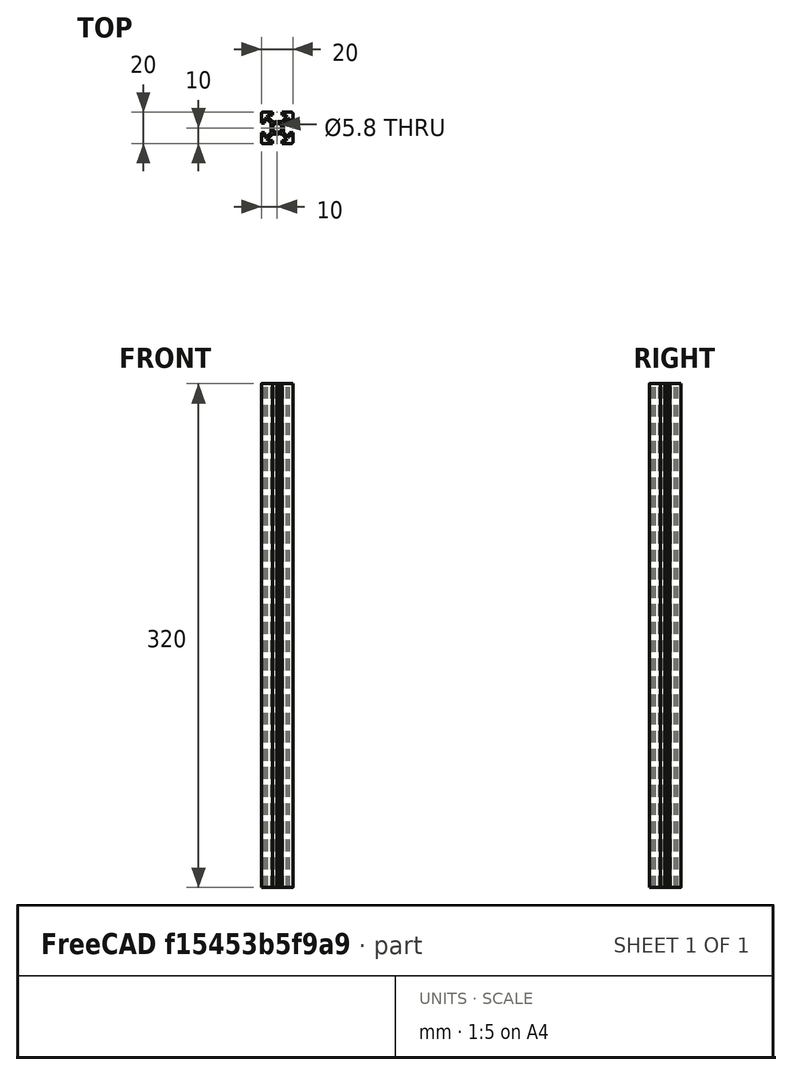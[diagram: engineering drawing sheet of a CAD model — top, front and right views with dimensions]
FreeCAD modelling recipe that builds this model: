
FCSTD DOCUMENT  (FreeCAD 0.17R13387 (Git))
Label: Y-Profile_2020
License: All rights reserved
LicenseURL: http://en.wikipedia.org/wiki/All_rights_reserved
objects: Sketcher::SketchObject×1, PartDesign::Pad×1, PartDesign::Body×1
note: 4 computed .brp shape members not serialized (recipe doc carries the construction recipe); baked Part::Feature solids carry a one-line shape summary decoded from their .brp

FEATURE [Sketcher::SketchObject] Sketch001
  sketch-geometry (77):
    g0: LineSegment StartX=-8 StartY=-3 StartZ=0 EndX=-10 EndY=-3 EndZ=0
    g1: LineSegment StartX=-10 StartY=-3 StartZ=0 EndX=-10 EndY=-9 EndZ=0
    g2: ArcOfCircle CenterX=-9 CenterY=-9 CenterZ=0 NormalX=0 NormalY=0 NormalZ=1 AngleXU=0 Radius=1 StartAngle=3.14159 EndAngle=4.71239
    g3: LineSegment StartX=-9 StartY=-10 StartZ=0 EndX=-3 EndY=-10 EndZ=0
    g4: LineSegment StartX=-3 StartY=-10 StartZ=0 EndX=-3 EndY=-8 EndZ=0
    g5: LineSegment StartX=-3 StartY=-8 StartZ=0 EndX=-6 EndY=-8 EndZ=0
    g6: LineSegment StartX=-6 StartY=-8 StartZ=0 EndX=-6 EndY=-7.06066 EndZ=0
    g7: LineSegment StartX=-6 StartY=-7.06066 StartZ=0 EndX=-2.93934 EndY=-4 EndZ=0
    g8: LineSegment StartX=-2.93934 StartY=-4 StartZ=0 EndX=-0.65359 EndY=-4 EndZ=0
    g9: ArcOfCircle CenterX=-0.65359 CenterY=-3.5 CenterZ=0 NormalX=0 NormalY=0 NormalZ=1 AngleXU=0 Radius=0.5 StartAngle=4.71239 EndAngle=5.23599
    g10: LineSegment StartX=-0.40359 StartY=-3.93301 StartZ=0 EndX=0 EndY=-3.7 EndZ=0
    g11: LineSegment StartX=0 StartY=-3.7 StartZ=0 EndX=0.40359 EndY=-3.93301 EndZ=0
    g12: ArcOfCircle CenterX=0.65359 CenterY=-3.5 CenterZ=0 NormalX=0 NormalY=0 NormalZ=1 AngleXU=0 Radius=0.5 StartAngle=4.18879 EndAngle=5.23599
    g13: LineSegment StartX=0.90359 StartY=-3.93301 StartZ=0 EndX=1.21889 EndY=-3.75098 EndZ=0
    g14: LineSegment StartX=1.21889 StartY=-3.75098 StartZ=0 EndX=2.5 EndY=-4 EndZ=0
    g15: LineSegment StartX=2.5 StartY=-4 StartZ=0 EndX=2.93934 EndY=-4 EndZ=0
    g16: LineSegment StartX=2.93934 StartY=-4 StartZ=0 EndX=6 EndY=-7.06066 EndZ=0
    g17: LineSegment StartX=6 StartY=-7.06066 StartZ=0 EndX=6 EndY=-8 EndZ=0
    g18: LineSegment StartX=6 StartY=-8 StartZ=0 EndX=3 EndY=-8 EndZ=0
    g19: LineSegment StartX=3 StartY=-8 StartZ=0 EndX=3 EndY=-10 EndZ=0
    g20: LineSegment StartX=3 StartY=-10 StartZ=0 EndX=9 EndY=-10 EndZ=0
    g21: ArcOfCircle CenterX=9 CenterY=-9 CenterZ=0 NormalX=0 NormalY=0 NormalZ=1 AngleXU=0 Radius=1 StartAngle=4.71239 EndAngle=6.28319
    g22: LineSegment StartX=10 StartY=-9 StartZ=0 EndX=10 EndY=-3 EndZ=0
    g23: LineSegment StartX=10 StartY=-3 StartZ=0 EndX=8 EndY=-3 EndZ=0
    g24: LineSegment StartX=8 StartY=-3 StartZ=0 EndX=8 EndY=-6 EndZ=0
    g25: LineSegment StartX=8 StartY=-6 StartZ=0 EndX=7.06066 EndY=-6 EndZ=0
    g26: LineSegment StartX=7.06066 StartY=-6 StartZ=0 EndX=4 EndY=-2.93934 EndZ=0
    g27: LineSegment StartX=4 StartY=-2.93934 StartZ=0 EndX=4 EndY=-0.65359 EndZ=0
    g28: ArcOfCircle CenterX=3.5 CenterY=-0.65359 CenterZ=0 NormalX=0 NormalY=0 NormalZ=1 AngleXU=0 Radius=0.5 StartAngle=0 EndAngle=0.523599
    g29: LineSegment StartX=3.93301 StartY=-0.40359 StartZ=0 EndX=3.7 EndY=0 EndZ=0
    g30: LineSegment StartX=3.7 StartY=0 StartZ=0 EndX=3.93301 EndY=0.40359 EndZ=0
    g31: ArcOfCircle CenterX=3.5 CenterY=0.65359 CenterZ=0 NormalX=0 NormalY=0 NormalZ=1 AngleXU=0 Radius=0.5 StartAngle=5.75959 EndAngle=6.80678
    g32: LineSegment StartX=3.93301 StartY=0.90359 StartZ=0 EndX=3.75098 EndY=1.21889 EndZ=0
    g33: LineSegment StartX=3.75098 StartY=1.21889 StartZ=0 EndX=4 EndY=2.5 EndZ=0
    g34: LineSegment StartX=4 StartY=2.5 StartZ=0 EndX=4 EndY=2.93934 EndZ=0
    g35: LineSegment StartX=4 StartY=2.93934 StartZ=0 EndX=7.06066 EndY=6 EndZ=0
    g36: LineSegment StartX=7.06066 StartY=6 StartZ=0 EndX=8 EndY=6 EndZ=0
    g37: LineSegment StartX=8 StartY=6 StartZ=0 EndX=8 EndY=3 EndZ=0
    g38: LineSegment StartX=8 StartY=3 StartZ=0 EndX=10 EndY=3 EndZ=0
    g39: LineSegment StartX=10 StartY=3 StartZ=0 EndX=10 EndY=9 EndZ=0
    g40: ArcOfCircle CenterX=9 CenterY=9 CenterZ=0 NormalX=0 NormalY=0 NormalZ=1 AngleXU=0 Radius=1 StartAngle=0 EndAngle=1.5708
    g41: LineSegment StartX=9 StartY=10 StartZ=0 EndX=3 EndY=10 EndZ=0
    g42: LineSegment StartX=3 StartY=10 StartZ=0 EndX=3 EndY=8 EndZ=0
    g43: LineSegment StartX=3 StartY=8 StartZ=0 EndX=6 EndY=8 EndZ=0
    g44: LineSegment StartX=6 StartY=8 StartZ=0 EndX=6 EndY=7.06066 EndZ=0
    g45: LineSegment StartX=6 StartY=7.06066 StartZ=0 EndX=2.93934 EndY=4 EndZ=0
    g46: LineSegment StartX=2.93934 StartY=4 StartZ=0 EndX=0.65359 EndY=4 EndZ=0
    g47: ArcOfCircle CenterX=0.65359 CenterY=3.5 CenterZ=0 NormalX=0 NormalY=0 NormalZ=1 AngleXU=0 Radius=0.5 StartAngle=1.5708 EndAngle=2.0944
    g48: LineSegment StartX=0.40359 StartY=3.93301 StartZ=0 EndX=0 EndY=3.7 EndZ=0
    g49: LineSegment StartX=0 StartY=3.7 StartZ=0 EndX=-0.40359 EndY=3.93301 EndZ=0
    g50: ArcOfCircle CenterX=-0.65359 CenterY=3.5 CenterZ=0 NormalX=0 NormalY=0 NormalZ=1 AngleXU=0 Radius=0.5 StartAngle=1.0472 EndAngle=2.0944
    g51: LineSegment StartX=-0.90359 StartY=3.93301 StartZ=0 EndX=-1.21889 EndY=3.75098 EndZ=0
    g52: LineSegment StartX=-1.21889 StartY=3.75098 StartZ=0 EndX=-2.5 EndY=4 EndZ=0
    g53: LineSegment StartX=-2.5 StartY=4 StartZ=0 EndX=-2.93934 EndY=4 EndZ=0
    g54: LineSegment StartX=-2.93934 StartY=4 StartZ=0 EndX=-6 EndY=7.06066 EndZ=0
    g55: LineSegment StartX=-6 StartY=7.06066 StartZ=0 EndX=-6 EndY=8 EndZ=0
    g56: LineSegment StartX=-6 StartY=8 StartZ=0 EndX=-3 EndY=8 EndZ=0
    g57: LineSegment StartX=-3 StartY=8 StartZ=0 EndX=-3 EndY=10 EndZ=0
    g58: LineSegment StartX=-3 StartY=10 StartZ=0 EndX=-9 EndY=10 EndZ=0
    g59: ArcOfCircle CenterX=-9 CenterY=9 CenterZ=0 NormalX=0 NormalY=0 NormalZ=1 AngleXU=0 Radius=1 StartAngle=1.5708 EndAngle=3.14159
    g60: LineSegment StartX=-10 StartY=9 StartZ=0 EndX=-10 EndY=3 EndZ=0
    g61: LineSegment StartX=-10 StartY=3 StartZ=0 EndX=-8 EndY=3 EndZ=0
    g62: LineSegment StartX=-8 StartY=3 StartZ=0 EndX=-8 EndY=6 EndZ=0
    g63: LineSegment StartX=-8 StartY=6 StartZ=0 EndX=-7.06066 EndY=6 EndZ=0
    g64: LineSegment StartX=-7.06066 StartY=6 StartZ=0 EndX=-4 EndY=2.93934 EndZ=0
    g65: LineSegment StartX=-4 StartY=2.93934 StartZ=0 EndX=-4 EndY=0.65359 EndZ=0
    g66: ArcOfCircle CenterX=-3.5 CenterY=0.65359 CenterZ=0 NormalX=0 NormalY=0 NormalZ=1 AngleXU=0 Radius=0.5 StartAngle=3.14159 EndAngle=3.66519
    g67: LineSegment StartX=-3.93301 StartY=0.40359 StartZ=0 EndX=-3.7 EndY=0 EndZ=0
    g68: LineSegment StartX=-3.7 StartY=0 StartZ=0 EndX=-3.93301 EndY=-0.40359 EndZ=0
    g69: ArcOfCircle CenterX=-3.5 CenterY=-0.65359 CenterZ=0 NormalX=0 NormalY=0 NormalZ=1 AngleXU=0 Radius=0.5 StartAngle=2.61799 EndAngle=3.66519
    g70: LineSegment StartX=-3.93301 StartY=-0.90359 StartZ=0 EndX=-3.75098 EndY=-1.21889 EndZ=0
    g71: LineSegment StartX=-3.75098 StartY=-1.21889 StartZ=0 EndX=-4 EndY=-2.5 EndZ=0
    g72: LineSegment StartX=-4 StartY=-2.5 StartZ=0 EndX=-4 EndY=-2.93934 EndZ=0
    g73: LineSegment StartX=-4 StartY=-2.93934 StartZ=0 EndX=-7.06066 EndY=-6 EndZ=0
    g74: LineSegment StartX=-7.06066 StartY=-6 StartZ=0 EndX=-8 EndY=-6 EndZ=0
    g75: LineSegment StartX=-8 StartY=-6 StartZ=0 EndX=-8 EndY=-3 EndZ=0
    g76: Circle CenterX=0 CenterY=0 CenterZ=0 NormalX=0 NormalY=0 NormalZ=1 AngleXU=0 Radius=2.9
  constraints (105):
    c: Horizontal(g0)
    c: Coincident(g0,g1)
    c: Vertical(g1)
    c: Coincident(g1,g2)
    c: Coincident(g2,g3)
    c: Horizontal(g3)
    c: Coincident(g3,g4)
    c: Coincident(g4,g5)
    c: Horizontal(g5)
    c: Coincident(g5,g6)
    c: Coincident(g6,g7)
    c: Coincident(g7,g8)
    c: Horizontal(g8)
    c: Coincident(g8,g9)
    c: Coincident(g9,g10)
    c: Coincident(g10,g11)
    c: Coincident(g11,g12)
    c: Coincident(g12,g13)
    c: Coincident(g13,g14)
    c: Coincident(g14,g15)
    c: Horizontal(g15)
    c: Coincident(g15,g16)
    c: Coincident(g16,g17)
    c: Coincident(g17,g18)
    c: Coincident(g18,g19)
    c: Vertical(g19)
    c: Coincident(g19,g20)
    c: Horizontal(g20)
    c: Coincident(g20,g21)
    c: Coincident(g21,g22)
    c: Vertical(g22)
    c: Coincident(g22,g23)
    c: Horizontal(g23)
    c: Coincident(g23,g24)
    c: Vertical(g24)
    c: Coincident(g24,g25)
    c: Coincident(g25,g26)
    c: Coincident(g26,g27)
    c: Vertical(g27)
    c: Coincident(g27,g28)
    c: Coincident(g28,g29)
    c: Coincident(g29,g30)
    c: Coincident(g30,g31)
    c: Coincident(g31,g32)
    c: Coincident(g32,g33)
    c: Coincident(g33,g34)
    c: Vertical(g34)
    c: Coincident(g34,g35)
    c: Coincident(g35,g36)
    c: Coincident(g36,g37)
    c: Coincident(g37,g38)
    c: Horizontal(g38)
    c: Coincident(g38,g39)
    c: Vertical(g39)
    c: Coincident(g39,g40)
    c: Coincident(g40,g41)
    c: Horizontal(g41)
    c: Coincident(g41,g42)
    c: Coincident(g42,g43)
    c: Horizontal(g43)
    c: Coincident(g43,g44)
    c: Coincident(g44,g45)
    c: Coincident(g45,g46)
    c: Horizontal(g46)
    c: Coincident(g46,g47)
    c: Coincident(g47,g48)
    c: Coincident(g48,g49)
    c: Coincident(g49,g50)
    c: Coincident(g50,g51)
    c: Coincident(g51,g52)
    c: Coincident(g52,g53)
    c: Horizontal(g53)
    c: Coincident(g53,g54)
    c: Coincident(g54,g55)
    c: Vertical(g55)
    c: Coincident(g55,g56)
    c: Coincident(g56,g57)
    c: Vertical(g57)
    c: Coincident(g57,g58)
    c: Horizontal(g58)
    c: Coincident(g58,g59)
    c: Coincident(g59,g60)
    c: Vertical(g60)
    c: Coincident(g60,g61)
    c: Horizontal(g61)
    c: Coincident(g61,g62)
    c: Vertical(g62)
    c: Coincident(g62,g63)
    c: Horizontal(g63)
    c: Coincident(g63,g64)
    c: Coincident(g64,g65)
    c: Vertical(g65)
    c: Coincident(g65,g66)
    c: Coincident(g66,g67)
    c: Coincident(g67,g68)
    c: Coincident(g68,g69)
    c: Coincident(g69,g70)
    c: Coincident(g70,g71)
    c: Coincident(g71,g72)
    c: Vertical(g72)
    c: Coincident(g72,g73)
    c: Coincident(g73,g74)
    c: Coincident(g74,g75)
    c: Coincident(g75,g0)
    c: Radius(g76) = 2.9
FEATURE [PartDesign::Pad] Pad
  Length = 320
  Length2 = 100
  Midplane = true
  Profile = -> Sketch001
  Type = 0
FEATURE [PartDesign::Body] Body
  Group = -> [Sketch001,Pad]
  Origin = -> Origin
  Tip = -> Pad
